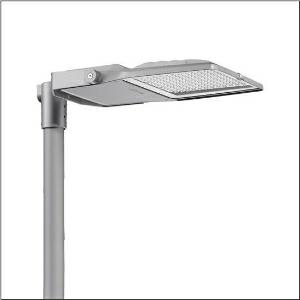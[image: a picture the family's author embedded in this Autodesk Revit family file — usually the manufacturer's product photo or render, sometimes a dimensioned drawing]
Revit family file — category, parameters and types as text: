
# Revit family: floodlight_fl_21_iq_midi___pl61_5xa7782f2c3a_b633
name_source: partatom
category: Lighting Fixtures
units: mm (PartAtom-declared; Revit-internal decimal feet)

## family parameters
Cut with Voids When Loaded = No
Host = Face
Light Source = No
Part Type = Normal
Room Calculation Point = No
Round Connector Dimension = Use Diameter
Shared = No

## types (1)
- --- (1 x LED, 35100 lm, 270.2 W, 3000K)
    Apparent Load = 270 VA
    CIE Flux Codes = 33 65 98 100 100
    Color Rendering = 70
    Color Temperature = 3000K
    Default Elevation = 1800 mm
    Description = Floodlight FL 21 iQ midi, floodlight, primary light control with lens, of PMMA, primary optical cover: protective disc, of toughened safety glass, transparent, light distribution: PL61, light emission: direct distribution, installation type: surface-mounted, lamps: LED, High Power LED, rated values: 35.100lm | 270,2W | 129,9lm/W (begin service life); end service life: 35.100lm | 286,6W; at 50% lumin. flux: 17.550lm | 117,4W | 149,5lm/W, colour temperature: 3000K, colour rendering: CRI > 70, light colour: 730, light setting 1 begin service life: 100% | 35.100lm | 270,2W | 129,9lm/W | 3.000K, light setting 1 end service life: 286,6W, further light settings possible, control: optimised constant luminous flux control (CLO 2.0), Desk-Remote (wireless, voltage-free reading and setting of iQ features in the workshop via application-optimized NFC function/RFID function), Smart-Wire, Night-Set, Temp-Guard, Auto-Match, Street-Remote, pre-setting: linear dimming characteristic, with terminal, 6-pole, mains connection: 220..240V, AC, 50/60Hz, luminaire housing, of diecast aluminium, powder-coated, SITECO metallic grey (DB 702S), corrosivity category C5 mid according to DIN EN ISO 12944suitable for swimming poolschlorine-resistant, sealing non-destructively replaceable, please order mast flange separately, mast bracket, of steel, galvanised, powder-coated, SITECO metallic grey (DB 702S), protection rating (complete): IP66, insulation class (complete): insulation class II (safety insulation), certification: CE, ENEC, VDE, protection symbol: D, impact resistance: IK08, permissible operating ambient temperature: -40..+40°C, permissible operating ambient temperature for outdoor applications: -40..+50°C, standard: DIN EN 12944, LABS conformity tested according to VDMA 24364:2018-05, packaging unit: 1 piece

Light Distribution: PL61
    Height = 76 mm
    Lamp = 1 x LED
    Lamp Light Flux = 35100 lm
    Lamp Power = 270.2 W
    Lamp count = 1
    Length = 657 mm
    Luminous efficacy = 130 lm/W
    Manufacturer = Siteco
    ModVariant = No
    Model = 5XA7782F2C3A
    Number of Poles = 1
    OnlyDefault = Yes
    Power Factor = 1
    Product Name = Floodlight FL 21 iQ midi | PL61
    Product group = floodlight | pylon annexe
    ProductGroupID = 6201
    Protection Class = Protection class II
    Protection Degree = IP 66
    RLX_Detail_Level = 1
    RLX_Emergency_Light_Flux = 0 lm
    RLX_Emergency_Type = 0
    RLX_Emergency_Type_DB = No
    RlxData = <blob elided: 153945 chars, md5=cfe8baf9>
    Socket = socket
    Standby Power = 0 W
    System Light Flux = 35100 lm
    System Power = 270 W
    Type Comments = factory setting: luminous flux: 100 % | dim-lin: 254 | 620 mA
    Type Image = l_1007123.jpg
    URL = http://relux.com
    VarID = @adj_108243
    Voltage = 0 V
    Weight = 0.00 kg
    Width = 442 mm

## geometry (parser evidence)
native form markers: Blend x4, Sweep x12
no freeform markers — native parametric forms only
